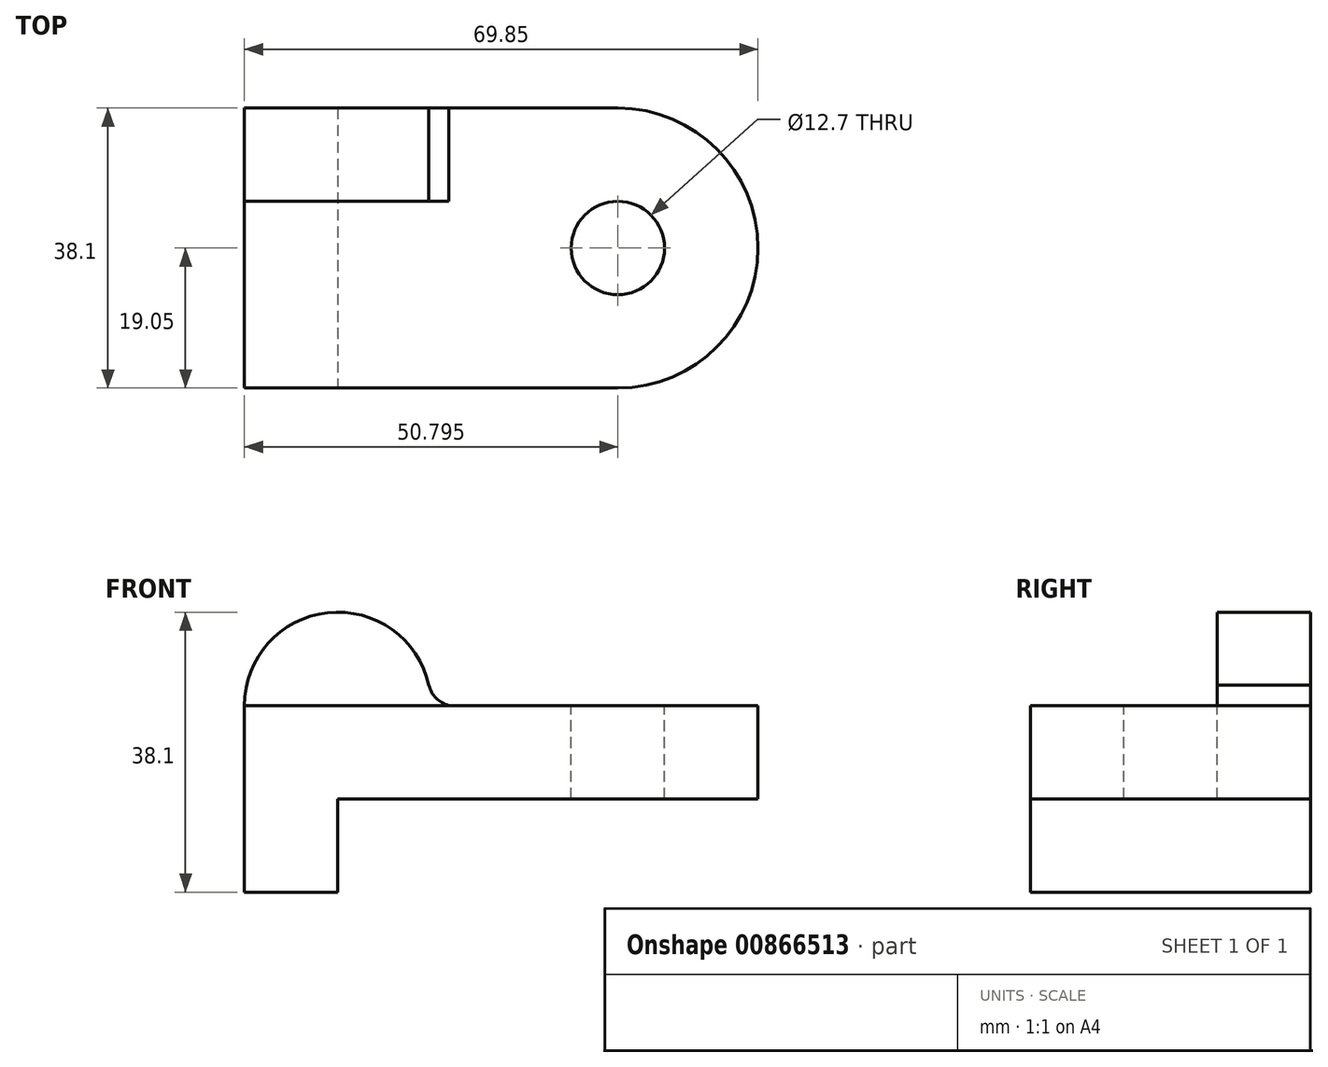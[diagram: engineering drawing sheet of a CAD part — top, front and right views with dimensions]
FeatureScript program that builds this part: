
annotation { "Feature Type Name" : "Feature", "Feature Type Description" : "" }
export const myFeature = defineFeature(function(context is Context, id is Id, definition is map)
    precondition{}
    {
        {
            var Q0;
            Q0=qCreatedBy(makeId("Top.planeOp"),FACE);
            var sketch = newSketch(context, id + "F0", { "sketchPlane" : qUnion([Q0])});
            skLineSegment(sketch, "E0.bottom", {"start": v(33.09, -1.05) * mm, "end": v(102.94, -1.05) * mm});
            skLineSegment(sketch, "E0.top", {"start": v(33.09, -39.15) * mm, "end": v(102.94, -39.15) * mm});
            skLineSegment(sketch, "E0.left", {"start": v(33.09, -1.05) * mm, "end": v(33.09, -39.15) * mm});
            skLineSegment(sketch, "E0.right", {"start": v(102.94, -1.05) * mm, "end": v(102.94, -39.15) * mm});
            skSolve(sketch);
        }
        {
            var Q0;
            Q0=makeQuery(id+"F0.imprint","IMPRINT",FACE,{"disambiguationData":[TD([[makeQuery(id+"F0.imprint","IMPRINT",EDGE,{"derivedFrom":sQuery(id+"F0.wireOp",EDGE,"E0.bottom")}),-1.0]])]});
            extrude(context, id + "F1", {"entities" : qUnion([Q0]), "depth" : 12.7 * mm, "offsetDistance" : 25.4 * mm});
        }
        {
            var Q0;
            Q0=makeQuery(id+"F1.opExtrude","SWEPT_FACE",FACE,{"disambiguationData":[OSD([sQuery(id+"F0.wireOp",EDGE,"E0.top")])]});
            var sketch = newSketch(context, id + "F2", { "sketchPlane" : qUnion([Q0])});
            skLineSegment(sketch, "E1.bottom", {"start": v(33.09, 0) * mm, "end": v(45.79, 0) * mm});
            skLineSegment(sketch, "E1.top", {"start": v(33.09, -12.7) * mm, "end": v(45.79, -12.7) * mm});
            skLineSegment(sketch, "E1.left", {"start": v(33.09, 0) * mm, "end": v(33.09, -12.7) * mm});
            skLineSegment(sketch, "E1.right", {"start": v(45.79, 0) * mm, "end": v(45.79, -12.7) * mm});
            skSolve(sketch);
        }
        {
            var Q0;
            Q0 = qSketchRegion(id + "F2", true);
            extrude(context, id + "F3", {"entities" : qUnion([Q0]), "operationType" : NewBodyOperationType.ADD, "oppositeDirection" : true, "depth" : 38.1 * mm, "offsetDistance" : 25.4 * mm});
        }
        {
            var Q0;
            Q0=makeQuery(id+"F1.opExtrude","CAP_FACE",FACE,{"disambiguationData":[OSD([sQuery(id+"F0.wireOp",EDGE,"E0.bottom"),sQuery(id+"F0.wireOp",EDGE,"E0.top"),sQuery(id+"F0.wireOp",EDGE,"E0.left"),sQuery(id+"F0.wireOp",EDGE,"E0.right")])],"isStart":false});
            var sketch = newSketch(context, id + "F4", { "sketchPlane" : qUnion([Q0])});
            skArc(sketch, "E2", {"start": v(102.94, -20.1) * mm, "mid": v(97.36, -6.63) * mm, "end": v(83.89, -1.05) * mm});
            skArc(sketch, "E3", {"start": v(83.89, -39.15) * mm, "mid": v(97.36, -33.57) * mm, "end": v(102.94, -20.1) * mm});
            skSolve(sketch);
        }
        {
            var Q0;
            {var subQ0=sQuery(id+"F4.wireOp",EDGE,"E2");Q0=makeQuery(id+"F4.imprint","IMPRINT",FACE,{"disambiguationData":[TD([[makeQuery(id+"F4.imprint","IMPRINT",EDGE,{"derivedFrom":subQ0}),-1.0]])]});}
            var Q1;
            {var subQ0=sQuery(id+"F4.wireOp",EDGE,"E3");Q1=makeQuery(id+"F4.imprint","IMPRINT",FACE,{"disambiguationData":[TD([[makeQuery(id+"F4.imprint","IMPRINT",EDGE,{"derivedFrom":subQ0}),-1.0]])]});}
            extrude(context, id + "F5", {"entities" : qUnion([Q0, Q1]), "operationType" : NewBodyOperationType.REMOVE, "oppositeDirection" : true, "depth" : 12.7 * mm, "offsetDistance" : 25.4 * mm});
        }
        {
            var Q0;
            Q0=makeQuery(id+"F1.opExtrude","CAP_FACE",FACE,{"disambiguationData":[OSD([sQuery(id+"F0.wireOp",EDGE,"E0.bottom"),sQuery(id+"F0.wireOp",EDGE,"E0.top"),sQuery(id+"F0.wireOp",EDGE,"E0.left"),sQuery(id+"F0.wireOp",EDGE,"E0.right")])],"isStart":false});
            var sketch = newSketch(context, id + "F6", { "sketchPlane" : qUnion([Q0])});
            skCircle(sketch, "E4", {"center": v(83.89, -20.1) * mm, "radius": 6.35 * mm});
            skSolve(sketch);
        }
        {
            var Q0;
            Q0 = qSketchRegion(id + "F6", true);
            extrude(context, id + "F7", {"entities" : qUnion([Q0]), "operationType" : NewBodyOperationType.REMOVE, "oppositeDirection" : true, "depth" : 12.7 * mm, "offsetDistance" : 25.4 * mm});
        }
        {
            var Q0;
            Q0=makeQuery(id+"F3.boolean.opBoolean","MERGE",FACE,{"derivedFrom":[makeQuery(id+"F1.opExtrude","SWEPT_FACE",FACE,{"disambiguationData":[OSD([sQuery(id+"F0.wireOp",EDGE,"E0.bottom")])]}),makeQuery(id+"F3.opExtrude","CAP_FACE",FACE,{"disambiguationData":[OSD([sQuery(id+"F2.wireOp",EDGE,"E1.bottom"),sQuery(id+"F2.wireOp",EDGE,"E1.top"),sQuery(id+"F2.wireOp",EDGE,"E1.left"),sQuery(id+"F2.wireOp",EDGE,"E1.right")])],"isStart":false})]});
            var sketch = newSketch(context, id + "F8", { "sketchPlane" : qUnion([Q0])});
            skArc(sketch, "E5", {"start": v(-33.09, 12.7) * mm, "mid": v(-45.79, 25.4) * mm, "end": v(-58.49, 12.7) * mm});
            skArc(sketch, "E6", {"start": v(-62.87, 12.7) * mm, "mid": v(-59.95, 13.1) * mm, "end": v(-58.18, 15.45) * mm});
            skSolve(sketch);
        }
        {
            var Q0;
            {var subQ3=sQuery(id+"F8.wireOp",EDGE,"E6");Q0=makeQuery(id+"F8.imprint","IMPRINT",FACE,{"disambiguationData":[TD([[makeQuery(id+"F8.imprint","IMPRINT",EDGE,{"derivedFrom":subQ3}),-1.0]])]});}
            var Q1;
            {var subQ0=sQuery(id+"F8.wireOp",EDGE,"E5");var subQ1=sQuery(id+"F0.wireOp",EDGE,"E0.bottom");var subQ2=makeQuery(id+"F1.opExtrude","CAP_EDGE",EDGE,{"disambiguationData":[OSD([subQ1])],"isStart":false});var subQ5=makeQuery(id+"F8.imprint","INTERSECT",VERTEX,{"derivedFrom":[subQ2,subQ0]});Q1=makeQuery(id+"F8.imprint","IMPRINT",FACE,{"disambiguationData":[TD([[makeQuery(id+"F8.imprint","IMPRINT",EDGE,{"disambiguationData":[TD([[subQ5,1.0]])],"derivedFrom":subQ0}),1.0]])]});}
            extrude(context, id + "F9", {"entities" : qUnion([Q0, Q1]), "operationType" : NewBodyOperationType.ADD, "oppositeDirection" : true, "depth" : 12.7 * mm, "offsetDistance" : 25.4 * mm});
        }
    });
